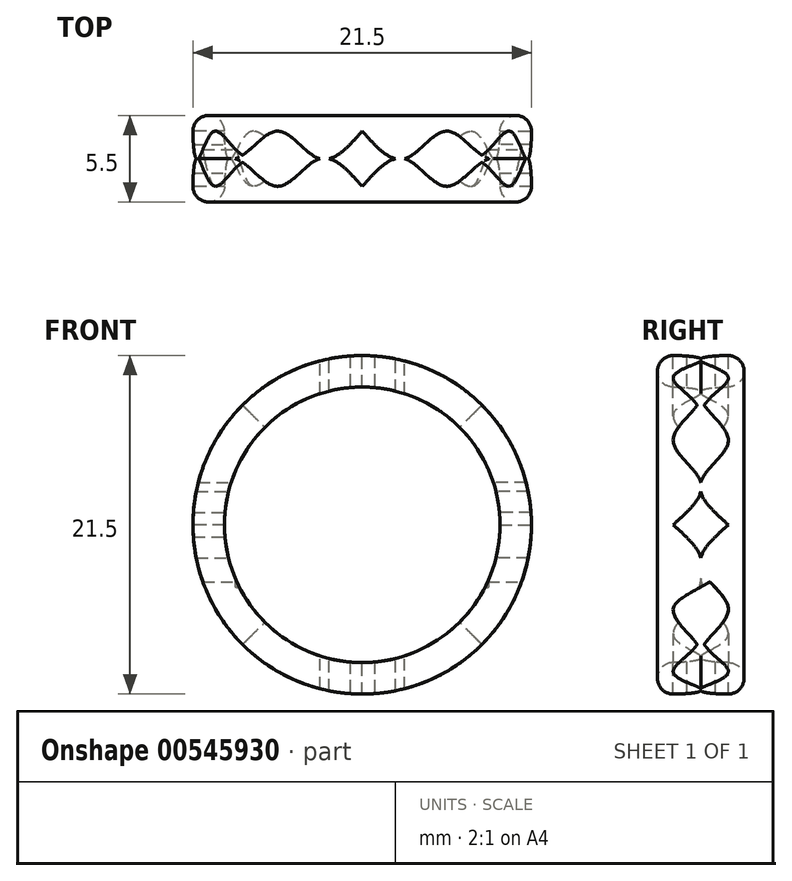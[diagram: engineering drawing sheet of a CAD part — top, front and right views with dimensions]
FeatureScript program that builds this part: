
annotation { "Feature Type Name" : "Feature", "Feature Type Description" : "" }
export const myFeature = defineFeature(function(context is Context, id is Id, definition is map)
    precondition{}
    {
        {
            var Q0;
            Q0=qCreatedBy(makeId("Front.planeOp"),FACE);
            var sketch = newSketch(context, id + "F0", { "sketchPlane" : qUnion([Q0])});
            skCircle(sketch, "E0", {"center": v(0, 0) * mm, "radius": 8.75 * mm});
            skCircle(sketch, "E1", {"center": v(0, 0) * mm, "radius": 10.75 * mm});
            skSolve(sketch);
        }
        {
            var Q0;
            Q0=makeQuery(id+"F0.imprint","IMPRINT",FACE,{"disambiguationData":[TD([[makeQuery(id+"F0.imprint","IMPRINT",EDGE,{"derivedFrom":sQuery(id+"F0.wireOp",EDGE,"E0")}),-1.0]])]});
            extrude(context, id + "F1", {"entities" : qUnion([Q0]), "depth" : 3.75 * mm, "offsetDistance" : 25 * mm, "hasSecondDirection" : true, "secondDirectionOppositeDirection" : true, "secondDirectionDepth" : 3.75 * mm});
        }
        {
            var Q0;
            Q0=makeQuery(id+"F1.opExtrude","CAP_EDGE",EDGE,{"disambiguationData":[OSD([sQuery(id+"F0.wireOp",EDGE,"E1")])],"isStart":false});
            var Q1;
            Q1=makeQuery(id+"F1.opExtrude","CAP_EDGE",EDGE,{"disambiguationData":[OSD([sQuery(id+"F0.wireOp",EDGE,"E1")])],"isStart":true});
            fillet(context, id + "F2", {"entities" : qUnion([Q0, Q1]), "radius" : 2 * mm, "tangentPropagation" : true, "allowEdgeOverflow" : false});
        }
        {
            var Q0;
            Q0=makeQuery(id+"F2.opFillet","BLEND_EDGE",EDGE,{"blendedFrom":[makeQuery(id+"F1.opExtrude","CAP_EDGE",EDGE,{"disambiguationData":[OSD([sQuery(id+"F0.wireOp",EDGE,"E1")])],"isStart":false}),makeQuery(id+"F1.opExtrude","SWEPT_FACE",FACE,{"disambiguationData":[OSD([sQuery(id+"F0.wireOp",EDGE,"E0")])]})],"blendedInto":[makeQuery(id+"F1.opExtrude","SWEPT_FACE",FACE,{"disambiguationData":[OSD([sQuery(id+"F0.wireOp",EDGE,"E0")])]})]});
            var Q1;
            Q1=makeQuery(id+"F2.opFillet","BLEND_EDGE",EDGE,{"blendedFrom":[makeQuery(id+"F1.opExtrude","CAP_EDGE",EDGE,{"disambiguationData":[OSD([sQuery(id+"F0.wireOp",EDGE,"E1")])],"isStart":true}),makeQuery(id+"F1.opExtrude","SWEPT_FACE",FACE,{"disambiguationData":[OSD([sQuery(id+"F0.wireOp",EDGE,"E0")])]})],"blendedInto":[makeQuery(id+"F1.opExtrude","SWEPT_FACE",FACE,{"disambiguationData":[OSD([sQuery(id+"F0.wireOp",EDGE,"E0")])]})]});
            fillet(context, id + "F3", {"entities" : qUnion([Q0, Q1]), "radius" : 1 * mm, "tangentPropagation" : true, "allowEdgeOverflow" : false});
        }
        {
            var Q0;
            Q0=qCreatedBy(makeId("Right.planeOp"),FACE);
            var sketch = newSketch(context, id + "F4", { "sketchPlane" : qUnion([Q0])});
            skLineSegment(sketch, "E2.bottom", {"start": v(1.75, -10.75) * mm, "end": v(-1.75, -10.75) * mm});
            skLineSegment(sketch, "E2.top", {"start": v(1.75, 10.75) * mm, "end": v(-1.75, 10.75) * mm});
            skLineSegment(sketch, "E2.left", {"start": v(1.75, -10.75) * mm, "end": v(1.75, 10.75) * mm});
            skLineSegment(sketch, "E2.right", {"start": v(-1.75, -10.75) * mm, "end": v(-1.75, 10.75) * mm});
            skPoint(sketch, "E2.middle", {"position": v(0, 0) * mm});
            skPoint(sketch, "E3", {"position": v(1.75, 5.38) * mm});
            skPoint(sketch, "E4", {"position": v(1.75, 2.69) * mm});
            skPoint(sketch, "E5", {"position": v(1.75, 8.06) * mm});
            skPoint(sketch, "E6.MirrorP", {"position": v(-1.75, 2.69) * mm});
            skPoint(sketch, "E7.MirrorP", {"position": v(-1.75, 5.38) * mm});
            skPoint(sketch, "E8.MirrorP", {"position": v(-1.75, 8.06) * mm});
            skPoint(sketch, "E9.MirrorP", {"position": v(-1.75, -2.69) * mm});
            skPoint(sketch, "E10.MirrorP", {"position": v(-1.75, -5.38) * mm});
            skPoint(sketch, "E11.MirrorP", {"position": v(-1.75, -8.06) * mm});
            skPoint(sketch, "E12.MirrorP", {"position": v(1.75, -8.06) * mm});
            skPoint(sketch, "E13.MirrorP", {"position": v(1.75, -5.38) * mm});
            skPoint(sketch, "E14.MirrorP", {"position": v(1.75, -2.69) * mm});
            skPoint(sketch, "E15", {"position": v(0, 8.06) * mm});
            skPoint(sketch, "E16", {"position": v(0, 5.38) * mm});
            skPoint(sketch, "E17", {"position": v(0, 2.69) * mm});
            skFitSpline(sketch, "E18", {"points": [v(0, 10.75) * mm, v(-1.75, 8.06) * mm, v(1.75, 5.38) * mm, v(-1.75, 2.69) * mm, v(0, 0) * mm], "startDerivative": vector(-14.8, -12.07) * mm, "endDerivative": vector(14.8, -12.08) * mm});
            skFitSpline(sketch, "E19.MirrorCS", {"points": [v(0, 10.75) * mm, v(1.75, 8.06) * mm, v(-1.75, 5.38) * mm, v(1.75, 2.69) * mm, v(0, 0) * mm], "startDerivative": vector(14.8, -12.07) * mm, "endDerivative": vector(-14.8, -12.08) * mm});
            skFitSpline(sketch, "E20.MirrorCS", {"points": [v(0, -10.75) * mm, v(-1.75, -8.06) * mm, v(1.75, -5.38) * mm, v(-1.75, -2.69) * mm, v(0, 0) * mm], "startDerivative": vector(-14.8, 12.07) * mm, "endDerivative": vector(14.8, 12.08) * mm});
            skFitSpline(sketch, "E21.MirrorCS", {"points": [v(0, -10.75) * mm, v(1.75, -8.06) * mm, v(-1.75, -5.38) * mm, v(1.75, -2.69) * mm, v(0, 0) * mm], "startDerivative": vector(14.8, 12.07) * mm, "endDerivative": vector(-14.8, 12.08) * mm});
            skFitSpline(sketch, "E22", {"points": [v(1.75, 10.75) * mm, v(0, 8.06) * mm, v(1.75, 5.38) * mm, v(0, 2.69) * mm, v(1.75, 0) * mm], "startDerivative": vector(-12, -10.75) * mm, "endDerivative": vector(12, -10.75) * mm});
            skFitSpline(sketch, "E23", {"points": [v(-1.75, 10.75) * mm, v(0, 8.06) * mm, v(-1.75, 5.38) * mm, v(0, 2.69) * mm, v(-1.75, 0) * mm], "startDerivative": vector(12, -10.75) * mm, "endDerivative": vector(-12, -10.75) * mm});
            skFitSpline(sketch, "E24.MirrorCS", {"points": [v(-1.75, -10.75) * mm, v(0, -8.06) * mm, v(-1.75, -5.38) * mm, v(0, -2.69) * mm, v(-1.75, 0) * mm], "startDerivative": vector(12, 10.75) * mm, "endDerivative": vector(-12, 10.75) * mm});
            skFitSpline(sketch, "E25.MirrorCS", {"points": [v(1.75, -10.75) * mm, v(0, -8.06) * mm, v(1.75, -5.38) * mm, v(0, -2.69) * mm, v(1.75, 0) * mm], "startDerivative": vector(-12, 10.75) * mm, "endDerivative": vector(12, 10.75) * mm});
            skSolve(sketch);
        }
        {
            var Q0;
            Q0=qCreatedBy(makeId("Top.planeOp"),FACE);
            cPlane(context, id + "F5", {"entities" : qUnion([Q0]), "cplaneType" : CPlaneType.OFFSET, "offset" : (21.5 / 2) * mm, "width" : 150 * mm, "height" : 150 * mm});
        }
        {
            var Q0;
            Q0=qCreatedBy(id+"F5.planeOp",FACE);
            var sketch = newSketch(context, id + "F6", { "sketchPlane" : qUnion([Q0])});
            skPoint(sketch, "E26", {"position": v(0, 0) * mm});
            skPoint(sketch, "E27", {"position": v(-10.75, 0) * mm});
            skPoint(sketch, "E28", {"position": v(0, -1.75) * mm});
            skPoint(sketch, "E29", {"position": v(-10.75, -1.75) * mm});
            skPoint(sketch, "E30", {"position": v(-10.75, 1.75) * mm});
            skPoint(sketch, "E31", {"position": v(0, 1.75) * mm});
            skPoint(sketch, "E32", {"position": v(-5.38, 1.75) * mm});
            skPoint(sketch, "E33", {"position": v(-8.06, 1.75) * mm});
            skPoint(sketch, "E34", {"position": v(-8.06, -1.75) * mm});
            skPoint(sketch, "E35", {"position": v(-5.38, -1.75) * mm});
            skPoint(sketch, "E36", {"position": v(-2.69, 1.75) * mm});
            skPoint(sketch, "E37", {"position": v(-2.69, -1.75) * mm});
            skPoint(sketch, "E38.MirrorP", {"position": v(10.75, -1.75) * mm});
            skPoint(sketch, "E39.MirrorP", {"position": v(10.75, 1.75) * mm});
            skPoint(sketch, "E40.MirrorP", {"position": v(10.75, 0) * mm});
            skPoint(sketch, "E41.MirrorP", {"position": v(8.06, -1.75) * mm});
            skPoint(sketch, "E42.MirrorP", {"position": v(8.06, 1.75) * mm});
            skPoint(sketch, "E43.MirrorP", {"position": v(5.38, 1.75) * mm});
            skPoint(sketch, "E44.MirrorP", {"position": v(2.69, 1.75) * mm});
            skPoint(sketch, "E45.MirrorP", {"position": v(2.69, -1.75) * mm});
            skPoint(sketch, "E46.MirrorP", {"position": v(5.38, -1.75) * mm});
            skPoint(sketch, "E47", {"position": v(-8.06, 0) * mm});
            skPoint(sketch, "E48", {"position": v(-5.38, 0) * mm});
            skPoint(sketch, "E49", {"position": v(-2.69, 0) * mm});
            skPoint(sketch, "E50.MirrorP", {"position": v(2.69, 0) * mm});
            skPoint(sketch, "E51.MirrorP", {"position": v(5.38, 0) * mm});
            skPoint(sketch, "E52.MirrorP", {"position": v(8.06, 0) * mm});
            skFitSpline(sketch, "E53", {"points": [v(0, 0) * mm, v(-2.69, -1.75) * mm, v(-5.38, 1.75) * mm, v(-8.06, -1.75) * mm, v(-10.75, 1.75) * mm], "startDerivative": vector(-12.6, -15.44) * mm, "endDerivative": vector(-10.32, 23.06) * mm});
            skFitSpline(sketch, "E54", {"points": [v(-10.75, -1.75) * mm, v(-8.06, 1.75) * mm, v(-5.38, -1.75) * mm, v(-2.69, 1.75) * mm, v(0, 0) * mm], "startDerivative": vector(13.87, 22.06) * mm, "endDerivative": vector(12.03, -14.48) * mm});
            skFitSpline(sketch, "E55", {"points": [v(0, 1.75) * mm, v(-2.69, 0) * mm, v(-5.38, 1.75) * mm, v(-8.06, 0) * mm, v(-10.75, 1.75) * mm], "startDerivative": vector(-10.75, -12) * mm, "endDerivative": vector(-10.75, 12) * mm});
            skFitSpline(sketch, "E56", {"points": [v(-10.75, -1.75) * mm, v(-8.06, 0) * mm, v(-5.38, -1.75) * mm, v(-2.69, 0) * mm, v(0, -1.75) * mm], "startDerivative": vector(10.75, 12) * mm, "endDerivative": vector(10.75, -12) * mm});
            skFitSpline(sketch, "E57.MirrorCS", {"points": [v(10.75, -1.75) * mm, v(8.06, 1.75) * mm, v(5.38, -1.75) * mm, v(2.69, 1.75) * mm, v(0, 0) * mm], "startDerivative": vector(-13.87, 22.06) * mm, "endDerivative": vector(-12.03, -14.48) * mm});
            skFitSpline(sketch, "E58.MirrorCS", {"points": [v(0, 0) * mm, v(2.69, -1.75) * mm, v(5.38, 1.75) * mm, v(8.06, -1.75) * mm, v(10.75, 1.75) * mm], "startDerivative": vector(12.6, -15.44) * mm, "endDerivative": vector(10.32, 23.06) * mm});
            skFitSpline(sketch, "E59.MirrorCS", {"points": [v(0, 1.75) * mm, v(2.69, 0) * mm, v(5.38, 1.75) * mm, v(8.06, 0) * mm, v(10.75, 1.75) * mm], "startDerivative": vector(10.75, -12) * mm, "endDerivative": vector(10.75, 12) * mm});
            skFitSpline(sketch, "E60.MirrorCS", {"points": [v(10.75, -1.75) * mm, v(8.06, 0) * mm, v(5.38, -1.75) * mm, v(2.69, 0) * mm, v(0, -1.75) * mm], "startDerivative": vector(-10.75, 12) * mm, "endDerivative": vector(-10.75, -12) * mm});
            skPoint(sketch, "E61", {"position": v(-4.48, -0.95) * mm});
            skPoint(sketch, "E62", {"position": v(-6.28, -0.95) * mm});
            skPoint(sketch, "E63.MirrorP", {"position": v(-6.28, 0.95) * mm});
            skPoint(sketch, "E64.MirrorP", {"position": v(-4.48, 0.95) * mm});
            skPoint(sketch, "E65.MirrorP", {"position": v(4.48, -0.95) * mm});
            skPoint(sketch, "E66.MirrorP", {"position": v(6.28, -0.95) * mm});
            skPoint(sketch, "E67.MirrorP", {"position": v(4.48, 0.95) * mm});
            skPoint(sketch, "E68.MirrorP", {"position": v(6.28, 0.95) * mm});
            skPoint(sketch, "E69", {"position": v(-5.38, -0.95) * mm});
            skLineSegment(sketch, "E70.left", {"start": v(10.75, -0.25) * mm, "end": v(10.75, 0.25) * mm});
            skLineSegment(sketch, "E70.right", {"start": v(-10.75, -0.25) * mm, "end": v(-10.75, 0.25) * mm});
            skSolve(sketch);
        }
        {
            var Q0;
            {var subQ3=sQuery(id+"F6.wireOp",EDGE,"E55");var subQ5=sQuery(id+"F6.wireOp",EDGE,"E59.MirrorCS");var subQ6=makeQuery(id+"F6.imprint","INTERSECT",VERTEX,{"derivedFrom":[subQ3,subQ5]});Q0=makeQuery(id+"F6.imprint","IMPRINT",FACE,{"disambiguationData":[TD([[makeQuery(id+"F6.imprint","IMPRINT",EDGE,{"disambiguationData":[TD([[subQ6,-1.0]])],"derivedFrom":subQ3}),1.0]])]});}
            var Q1;
            {var subQ1=sQuery(id+"F6.wireOp",EDGE,"E57.MirrorCS");var subQ3=sQuery(id+"F6.wireOp",EDGE,"E59.MirrorCS");var subQ4=makeQuery(id+"F6.imprint","INTERSECT",VERTEX,{"disambiguationData":[OD(3.0)],"derivedFrom":[subQ1,subQ3]});Q1=makeQuery(id+"F6.imprint","IMPRINT",FACE,{"disambiguationData":[TD([[makeQuery(id+"F6.imprint","IMPRINT",EDGE,{"disambiguationData":[TD([[subQ4,-1.0]])],"derivedFrom":subQ3}),-1.0]])]});}
            var Q2;
            {var subQ3=sQuery(id+"F6.wireOp",EDGE,"E56");var subQ5=sQuery(id+"F6.wireOp",EDGE,"E60.MirrorCS");var subQ6=makeQuery(id+"F6.imprint","INTERSECT",VERTEX,{"derivedFrom":[subQ3,subQ5]});Q2=makeQuery(id+"F6.imprint","IMPRINT",FACE,{"disambiguationData":[TD([[makeQuery(id+"F6.imprint","IMPRINT",EDGE,{"disambiguationData":[TD([[subQ6,1.0]])],"derivedFrom":subQ3}),1.0]])]});}
            var Q3;
            {var subQ0=sQuery(id+"F6.wireOp",EDGE,"E54");var subQ5=sQuery(id+"F6.wireOp",EDGE,"E55");var subQ7=makeQuery(id+"F6.imprint","INTERSECT",VERTEX,{"disambiguationData":[OD(3.0)],"derivedFrom":[subQ0,subQ5]});Q3=makeQuery(id+"F6.imprint","IMPRINT",FACE,{"disambiguationData":[TD([[makeQuery(id+"F6.imprint","IMPRINT",EDGE,{"disambiguationData":[TD([[subQ7,-1.0]])],"derivedFrom":subQ5}),1.0]])]});}
            var Q4;
            {var subQ0=sQuery(id+"F6.wireOp",EDGE,"E56");var subQ1=sQuery(id+"F6.wireOp",EDGE,"E53");var subQ2=makeQuery(id+"F6.imprint","INTERSECT",VERTEX,{"disambiguationData":[OD(1.0)],"derivedFrom":[subQ1,subQ0]});Q4=makeQuery(id+"F6.imprint","IMPRINT",FACE,{"disambiguationData":[TD([[makeQuery(id+"F6.imprint","IMPRINT",EDGE,{"disambiguationData":[TD([[subQ2,-1.0]])],"derivedFrom":subQ1}),-1.0]])]});}
            var Q5;
            {var subQ0=sQuery(id+"F6.wireOp",EDGE,"E55");var subQ1=sQuery(id+"F6.wireOp",EDGE,"E53");var subQ2=makeQuery(id+"F6.imprint","INTERSECT",VERTEX,{"disambiguationData":[OD(1.0)],"derivedFrom":[subQ1,subQ0]});Q5=makeQuery(id+"F6.imprint","IMPRINT",FACE,{"disambiguationData":[TD([[makeQuery(id+"F6.imprint","IMPRINT",EDGE,{"disambiguationData":[TD([[subQ2,1.0]])],"derivedFrom":subQ1}),-1.0]])]});}
            var Q6;
            {var subQ0=sQuery(id+"F6.wireOp",EDGE,"E56");var subQ1=sQuery(id+"F6.wireOp",EDGE,"E53");var subQ2=makeQuery(id+"F6.imprint","INTERSECT",VERTEX,{"disambiguationData":[OD(1.0)],"derivedFrom":[subQ1,subQ0]});Q6=makeQuery(id+"F6.imprint","IMPRINT",FACE,{"disambiguationData":[TD([[makeQuery(id+"F6.imprint","IMPRINT",EDGE,{"disambiguationData":[TD([[subQ2,-1.0]])],"derivedFrom":subQ1}),1.0]])]});}
            var Q7;
            {var subQ0=sQuery(id+"F6.wireOp",EDGE,"E59.MirrorCS");var subQ1=sQuery(id+"F6.wireOp",EDGE,"E57.MirrorCS");var subQ2=makeQuery(id+"F6.imprint","INTERSECT",VERTEX,{"disambiguationData":[OD(2.0)],"derivedFrom":[subQ1,subQ0]});Q7=makeQuery(id+"F6.imprint","IMPRINT",FACE,{"disambiguationData":[TD([[makeQuery(id+"F6.imprint","IMPRINT",EDGE,{"disambiguationData":[TD([[subQ2,1.0]])],"derivedFrom":subQ1}),1.0]])]});}
            var Q8;
            {var subQ0=sQuery(id+"F6.wireOp",EDGE,"E59.MirrorCS");var subQ1=sQuery(id+"F6.wireOp",EDGE,"E57.MirrorCS");var subQ2=makeQuery(id+"F6.imprint","INTERSECT",VERTEX,{"disambiguationData":[OD(2.0)],"derivedFrom":[subQ1,subQ0]});Q8=makeQuery(id+"F6.imprint","IMPRINT",FACE,{"disambiguationData":[TD([[makeQuery(id+"F6.imprint","IMPRINT",EDGE,{"disambiguationData":[TD([[subQ2,1.0]])],"derivedFrom":subQ1}),-1.0]])]});}
            var Q9;
            {var subQ0=sQuery(id+"F6.wireOp",EDGE,"E60.MirrorCS");var subQ1=sQuery(id+"F6.wireOp",EDGE,"E57.MirrorCS");var subQ2=makeQuery(id+"F6.imprint","INTERSECT",VERTEX,{"disambiguationData":[OD(2.0)],"derivedFrom":[subQ1,subQ0]});Q9=makeQuery(id+"F6.imprint","IMPRINT",FACE,{"disambiguationData":[TD([[makeQuery(id+"F6.imprint","IMPRINT",EDGE,{"disambiguationData":[TD([[subQ2,-1.0]])],"derivedFrom":subQ1}),1.0]])]});}
            var Q10;
            {var subQ0=sQuery(id+"F6.wireOp",EDGE,"E55");var subQ1=sQuery(id+"F6.wireOp",EDGE,"E53");var subQ2=makeQuery(id+"F6.imprint","INTERSECT",VERTEX,{"disambiguationData":[OD(2.0)],"derivedFrom":[subQ1,subQ0]});Q10=makeQuery(id+"F6.imprint","IMPRINT",FACE,{"disambiguationData":[TD([[makeQuery(id+"F6.imprint","IMPRINT",EDGE,{"disambiguationData":[TD([[subQ2,-1.0]])],"derivedFrom":subQ1}),-1.0]])]});}
            var Q11;
            {var subQ0=sQuery(id+"F6.wireOp",EDGE,"E56");var subQ1=sQuery(id+"F6.wireOp",EDGE,"E53");var subQ2=makeQuery(id+"F6.imprint","INTERSECT",VERTEX,{"disambiguationData":[OD(2.0)],"derivedFrom":[subQ1,subQ0]});Q11=makeQuery(id+"F6.imprint","IMPRINT",FACE,{"disambiguationData":[TD([[makeQuery(id+"F6.imprint","IMPRINT",EDGE,{"disambiguationData":[TD([[subQ2,1.0]])],"derivedFrom":subQ1}),-1.0]])]});}
            var Q12;
            {var subQ0=sQuery(id+"F6.wireOp",EDGE,"E56");var subQ1=sQuery(id+"F6.wireOp",EDGE,"E53");var subQ2=makeQuery(id+"F6.imprint","INTERSECT",VERTEX,{"disambiguationData":[OD(2.0)],"derivedFrom":[subQ1,subQ0]});Q12=makeQuery(id+"F6.imprint","IMPRINT",FACE,{"disambiguationData":[TD([[makeQuery(id+"F6.imprint","IMPRINT",EDGE,{"disambiguationData":[TD([[subQ2,1.0]])],"derivedFrom":subQ1}),1.0]])]});}
            var Q13;
            {var subQ0=sQuery(id+"F6.wireOp",EDGE,"E60.MirrorCS");var subQ1=sQuery(id+"F6.wireOp",EDGE,"E57.MirrorCS");var subQ2=makeQuery(id+"F6.imprint","INTERSECT",VERTEX,{"disambiguationData":[OD(1.0)],"derivedFrom":[subQ1,subQ0]});Q13=makeQuery(id+"F6.imprint","IMPRINT",FACE,{"disambiguationData":[TD([[makeQuery(id+"F6.imprint","IMPRINT",EDGE,{"disambiguationData":[TD([[subQ2,1.0]])],"derivedFrom":subQ1}),1.0]])]});}
            var Q14;
            {var subQ0=sQuery(id+"F6.wireOp",EDGE,"E59.MirrorCS");var subQ1=sQuery(id+"F6.wireOp",EDGE,"E57.MirrorCS");var subQ2=makeQuery(id+"F6.imprint","INTERSECT",VERTEX,{"disambiguationData":[OD(1.0)],"derivedFrom":[subQ1,subQ0]});Q14=makeQuery(id+"F6.imprint","IMPRINT",FACE,{"disambiguationData":[TD([[makeQuery(id+"F6.imprint","IMPRINT",EDGE,{"disambiguationData":[TD([[subQ2,-1.0]])],"derivedFrom":subQ1}),1.0]])]});}
            var Q15;
            {var subQ0=sQuery(id+"F6.wireOp",EDGE,"E59.MirrorCS");var subQ1=sQuery(id+"F6.wireOp",EDGE,"E57.MirrorCS");var subQ2=makeQuery(id+"F6.imprint","INTERSECT",VERTEX,{"disambiguationData":[OD(1.0)],"derivedFrom":[subQ1,subQ0]});Q15=makeQuery(id+"F6.imprint","IMPRINT",FACE,{"disambiguationData":[TD([[makeQuery(id+"F6.imprint","IMPRINT",EDGE,{"disambiguationData":[TD([[subQ2,-1.0]])],"derivedFrom":subQ1}),-1.0]])]});}
            var Q16;
            {var subQ3=sQuery(id+"F6.wireOp",EDGE,"E53");var subQ5=sQuery(id+"F6.wireOp",EDGE,"E55");var subQ9=makeQuery(id+"F6.imprint","INTERSECT",VERTEX,{"disambiguationData":[OD(1.0)],"derivedFrom":[subQ3,subQ5]});Q16=makeQuery(id+"F6.imprint","IMPRINT",FACE,{"disambiguationData":[TD([[makeQuery(id+"F6.imprint","IMPRINT",EDGE,{"disambiguationData":[TD([[subQ9,1.0]])],"derivedFrom":subQ3}),1.0]])]});}
            var Q17;
            {var subQ3=sQuery(id+"F6.wireOp",EDGE,"E57.MirrorCS");var subQ5=sQuery(id+"F6.wireOp",EDGE,"E60.MirrorCS");var subQ6=makeQuery(id+"F6.imprint","INTERSECT",VERTEX,{"disambiguationData":[OD(1.0)],"derivedFrom":[subQ3,subQ5]});Q17=makeQuery(id+"F6.imprint","IMPRINT",FACE,{"disambiguationData":[TD([[makeQuery(id+"F6.imprint","IMPRINT",EDGE,{"disambiguationData":[TD([[subQ6,1.0]])],"derivedFrom":subQ3}),-1.0]])]});}
            var Q18;
            {var subQ0=sQuery(id+"F6.wireOp",EDGE,"E56");var subQ1=sQuery(id+"F6.wireOp",EDGE,"E53");var subQ2=makeQuery(id+"F6.imprint","INTERSECT",VERTEX,{"disambiguationData":[OD(0.0)],"derivedFrom":[subQ1,subQ0]});Q18=makeQuery(id+"F6.imprint","IMPRINT",FACE,{"disambiguationData":[TD([[makeQuery(id+"F6.imprint","IMPRINT",EDGE,{"disambiguationData":[TD([[subQ2,1.0]])],"derivedFrom":subQ1}),-1.0]])]});}
            var Q19;
            Q19=makeQuery(id+"FG5QF2xXgg8FTiy_1.imprint","IMPRINT",FACE,{"disambiguationData":[TD([[makeQuery(id+"FG5QF2xXgg8FTiy_1.imprint","IMPRINT",EDGE,{"derivedFrom":sQuery(id+"FG5QF2xXgg8FTiy_1.wireOp",EDGE,"0z52b0YR-wwrJ-KUp3-x6KW-sjqR8KIbK8CL.bottom")}),-1.0]])]});
            var Q20;
            {var subQ0=sQuery(id+"F6.wireOp",EDGE,"E60.MirrorCS");var subQ1=sQuery(id+"F6.wireOp",EDGE,"E58.MirrorCS");var subQ2=makeQuery(id+"F6.imprint","INTERSECT",VERTEX,{"disambiguationData":[OD(0.0)],"derivedFrom":[subQ1,subQ0]});Q20=makeQuery(id+"F6.imprint","IMPRINT",FACE,{"disambiguationData":[TD([[makeQuery(id+"F6.imprint","IMPRINT",EDGE,{"disambiguationData":[TD([[subQ2,1.0]])],"derivedFrom":subQ1}),1.0]])]});}
            var Q21;
            {var subQ0=sQuery(id+"F6.wireOp",EDGE,"E56");var subQ1=sQuery(id+"F6.wireOp",EDGE,"E54");var subQ2=makeQuery(id+"F6.imprint","INTERSECT",VERTEX,{"disambiguationData":[OD(1.0)],"derivedFrom":[subQ1,subQ0]});Q21=makeQuery(id+"F6.imprint","IMPRINT",FACE,{"disambiguationData":[TD([[makeQuery(id+"F6.imprint","IMPRINT",EDGE,{"disambiguationData":[TD([[subQ2,1.0]])],"derivedFrom":subQ1}),1.0]])]});}
            var Q22;
            {var subQ0=sQuery(id+"F6.wireOp",EDGE,"E59.MirrorCS");var subQ1=sQuery(id+"F6.wireOp",EDGE,"E58.MirrorCS");var subQ2=makeQuery(id+"F6.imprint","INTERSECT",VERTEX,{"disambiguationData":[OD(1.0)],"derivedFrom":[subQ1,subQ0]});Q22=makeQuery(id+"F6.imprint","IMPRINT",FACE,{"disambiguationData":[TD([[makeQuery(id+"F6.imprint","IMPRINT",EDGE,{"disambiguationData":[TD([[subQ2,1.0]])],"derivedFrom":subQ1}),-1.0]])]});}
            var Q23;
            {var subQ0=sQuery(id+"F6.wireOp",EDGE,"E60.MirrorCS");var subQ1=sQuery(id+"F6.wireOp",EDGE,"E58.MirrorCS");var subQ2=makeQuery(id+"F6.imprint","INTERSECT",VERTEX,{"disambiguationData":[OD(1.0)],"derivedFrom":[subQ1,subQ0]});Q23=makeQuery(id+"F6.imprint","IMPRINT",FACE,{"disambiguationData":[TD([[makeQuery(id+"F6.imprint","IMPRINT",EDGE,{"disambiguationData":[TD([[subQ2,-1.0]])],"derivedFrom":subQ1}),1.0]])]});}
            var Q24;
            {var subQ0=sQuery(id+"F6.wireOp",EDGE,"E60.MirrorCS");var subQ1=sQuery(id+"F6.wireOp",EDGE,"E58.MirrorCS");var subQ2=makeQuery(id+"F6.imprint","INTERSECT",VERTEX,{"disambiguationData":[OD(2.0)],"derivedFrom":[subQ1,subQ0]});Q24=makeQuery(id+"F6.imprint","IMPRINT",FACE,{"disambiguationData":[TD([[makeQuery(id+"F6.imprint","IMPRINT",EDGE,{"disambiguationData":[TD([[subQ2,1.0]])],"derivedFrom":subQ1}),1.0]])]});}
            var Q25;
            {var subQ0=sQuery(id+"F6.wireOp",EDGE,"E55");var subQ1=sQuery(id+"F6.wireOp",EDGE,"E54");var subQ2=makeQuery(id+"F6.imprint","INTERSECT",VERTEX,{"disambiguationData":[OD(2.0)],"derivedFrom":[subQ1,subQ0]});Q25=makeQuery(id+"F6.imprint","IMPRINT",FACE,{"disambiguationData":[TD([[makeQuery(id+"F6.imprint","IMPRINT",EDGE,{"disambiguationData":[TD([[subQ2,1.0]])],"derivedFrom":subQ1}),-1.0]])]});}
            var Q26;
            {var subQ0=sQuery(id+"F6.wireOp",EDGE,"E55");var subQ1=sQuery(id+"F6.wireOp",EDGE,"E54");var subQ2=makeQuery(id+"F6.imprint","INTERSECT",VERTEX,{"disambiguationData":[OD(1.0)],"derivedFrom":[subQ1,subQ0]});Q26=makeQuery(id+"F6.imprint","IMPRINT",FACE,{"disambiguationData":[TD([[makeQuery(id+"F6.imprint","IMPRINT",EDGE,{"disambiguationData":[TD([[subQ2,-1.0]])],"derivedFrom":subQ1}),-1.0]])]});}
            extrude(context, id + "F7", {"entities" : qUnion([Q0, Q1, Q2, Q3, Q4, Q5, Q6, Q7, Q8, Q9, Q10, Q11, Q12, Q13, Q14, Q15, Q16, Q17, Q18, Q19, Q20, Q21, Q22, Q23, Q24, Q25, Q26]), "operationType" : NewBodyOperationType.REMOVE, "oppositeDirection" : true, "depth" : 25 * mm, "offsetDistance" : 25 * mm});
        }
        {
            var Q0;
            {var subQ0=sQuery(id+"F4.wireOp",EDGE,"E19.MirrorCS");var subQ5=sQuery(id+"F4.wireOp",EDGE,"E22");var subQ6=makeQuery(id+"F4.imprint","INTERSECT",VERTEX,{"disambiguationData":[OD(3.0)],"derivedFrom":[subQ0,subQ5]});Q0=makeQuery(id+"F4.imprint","IMPRINT",FACE,{"disambiguationData":[TD([[makeQuery(id+"F4.imprint","IMPRINT",EDGE,{"disambiguationData":[TD([[subQ6,1.0]])],"derivedFrom":subQ5}),-1.0]])]});}
            var Q1;
            {var subQ1=sQuery(id+"F4.wireOp",EDGE,"E18");var subQ3=sQuery(id+"F4.wireOp",EDGE,"E23");var subQ4=makeQuery(id+"F4.imprint","INTERSECT",VERTEX,{"disambiguationData":[OD(3.0)],"derivedFrom":[subQ1,subQ3]});Q1=makeQuery(id+"F4.imprint","IMPRINT",FACE,{"disambiguationData":[TD([[makeQuery(id+"F4.imprint","IMPRINT",EDGE,{"disambiguationData":[TD([[subQ4,-1.0]])],"derivedFrom":subQ3}),1.0]])]});}
            var Q2;
            {var subQ1=sQuery(id+"F4.wireOp",EDGE,"E20.MirrorCS");var subQ3=sQuery(id+"F4.wireOp",EDGE,"E24.MirrorCS");var subQ4=makeQuery(id+"F4.imprint","INTERSECT",VERTEX,{"disambiguationData":[OD(3.0)],"derivedFrom":[subQ1,subQ3]});Q2=makeQuery(id+"F4.imprint","IMPRINT",FACE,{"disambiguationData":[TD([[makeQuery(id+"F4.imprint","IMPRINT",EDGE,{"disambiguationData":[TD([[subQ4,1.0]])],"derivedFrom":subQ3}),-1.0]])]});}
            var Q3;
            {var subQ1=sQuery(id+"F4.wireOp",EDGE,"E19.MirrorCS");var subQ3=sQuery(id+"F4.wireOp",EDGE,"E22");var subQ4=makeQuery(id+"F4.imprint","INTERSECT",VERTEX,{"disambiguationData":[OD(3.0)],"derivedFrom":[subQ1,subQ3]});Q3=makeQuery(id+"F4.imprint","IMPRINT",FACE,{"disambiguationData":[TD([[makeQuery(id+"F4.imprint","IMPRINT",EDGE,{"disambiguationData":[TD([[subQ4,-1.0]])],"derivedFrom":subQ3}),-1.0]])]});}
            var Q4;
            {var subQ0=sQuery(id+"F4.wireOp",EDGE,"E19.MirrorCS");var subQ1=sQuery(id+"F4.wireOp",EDGE,"E18");var subQ2=makeQuery(id+"F4.imprint","INTERSECT",VERTEX,{"disambiguationData":[OD(1.0)],"derivedFrom":[subQ1,subQ0]});Q4=makeQuery(id+"F4.imprint","IMPRINT",FACE,{"disambiguationData":[TD([[makeQuery(id+"F4.imprint","IMPRINT",EDGE,{"disambiguationData":[TD([[subQ2,-1.0]])],"derivedFrom":subQ1}),1.0]])]});}
            var Q5;
            {var subQ0=sQuery(id+"F4.wireOp",EDGE,"E19.MirrorCS");var subQ1=sQuery(id+"F4.wireOp",EDGE,"E18");var subQ2=makeQuery(id+"F4.imprint","INTERSECT",VERTEX,{"disambiguationData":[OD(1.0)],"derivedFrom":[subQ1,subQ0]});Q5=makeQuery(id+"F4.imprint","IMPRINT",FACE,{"disambiguationData":[TD([[makeQuery(id+"F4.imprint","IMPRINT",EDGE,{"disambiguationData":[TD([[subQ2,-1.0]])],"derivedFrom":subQ1}),-1.0]])]});}
            var Q6;
            {var subQ0=sQuery(id+"F4.wireOp",EDGE,"E22");var subQ1=sQuery(id+"F4.wireOp",EDGE,"E18");var subQ2=makeQuery(id+"F4.imprint","INTERSECT",VERTEX,{"derivedFrom":[subQ1,subQ0]});Q6=makeQuery(id+"F4.imprint","IMPRINT",FACE,{"disambiguationData":[TD([[makeQuery(id+"F4.imprint","IMPRINT",EDGE,{"disambiguationData":[TD([[subQ2,-1.0]])],"derivedFrom":subQ1}),1.0]])]});}
            var Q7;
            {var subQ0=sQuery(id+"F4.wireOp",EDGE,"E21.MirrorCS");var subQ1=sQuery(id+"F4.wireOp",EDGE,"E20.MirrorCS");var subQ2=makeQuery(id+"F4.imprint","INTERSECT",VERTEX,{"disambiguationData":[OD(1.0)],"derivedFrom":[subQ1,subQ0]});Q7=makeQuery(id+"F4.imprint","IMPRINT",FACE,{"disambiguationData":[TD([[makeQuery(id+"F4.imprint","IMPRINT",EDGE,{"disambiguationData":[TD([[subQ2,-1.0]])],"derivedFrom":subQ1}),-1.0]])]});}
            var Q8;
            {var subQ0=sQuery(id+"F4.wireOp",EDGE,"E21.MirrorCS");var subQ1=sQuery(id+"F4.wireOp",EDGE,"E20.MirrorCS");var subQ2=makeQuery(id+"F4.imprint","INTERSECT",VERTEX,{"disambiguationData":[OD(1.0)],"derivedFrom":[subQ1,subQ0]});Q8=makeQuery(id+"F4.imprint","IMPRINT",FACE,{"disambiguationData":[TD([[makeQuery(id+"F4.imprint","IMPRINT",EDGE,{"disambiguationData":[TD([[subQ2,-1.0]])],"derivedFrom":subQ1}),1.0]])]});}
            var Q9;
            {var subQ0=sQuery(id+"F4.wireOp",EDGE,"E25.MirrorCS");var subQ1=sQuery(id+"F4.wireOp",EDGE,"E20.MirrorCS");var subQ2=makeQuery(id+"F4.imprint","INTERSECT",VERTEX,{"derivedFrom":[subQ1,subQ0]});Q9=makeQuery(id+"F4.imprint","IMPRINT",FACE,{"disambiguationData":[TD([[makeQuery(id+"F4.imprint","IMPRINT",EDGE,{"disambiguationData":[TD([[subQ2,-1.0]])],"derivedFrom":subQ1}),-1.0]])]});}
            var Q10;
            {var subQ0=sQuery(id+"F4.wireOp",EDGE,"E24.MirrorCS");var subQ1=sQuery(id+"F4.wireOp",EDGE,"E20.MirrorCS");var subQ2=makeQuery(id+"F4.imprint","INTERSECT",VERTEX,{"disambiguationData":[OD(1.0)],"derivedFrom":[subQ1,subQ0]});Q10=makeQuery(id+"F4.imprint","IMPRINT",FACE,{"disambiguationData":[TD([[makeQuery(id+"F4.imprint","IMPRINT",EDGE,{"disambiguationData":[TD([[subQ2,-1.0]])],"derivedFrom":subQ1}),1.0]])]});}
            var Q11;
            {var subQ1=sQuery(id+"F4.wireOp",EDGE,"E20.MirrorCS");var subQ3=sQuery(id+"F4.wireOp",EDGE,"E21.MirrorCS");var subQ4=makeQuery(id+"F4.imprint","INTERSECT",VERTEX,{"disambiguationData":[OD(0.0)],"derivedFrom":[subQ1,subQ3]});Q11=makeQuery(id+"F4.imprint","IMPRINT",FACE,{"disambiguationData":[TD([[makeQuery(id+"F4.imprint","IMPRINT",EDGE,{"disambiguationData":[TD([[subQ4,1.0]])],"derivedFrom":subQ3}),-1.0]])]});}
            var Q12;
            {var subQ0=sQuery(id+"F4.wireOp",EDGE,"E24.MirrorCS");var subQ1=sQuery(id+"F4.wireOp",EDGE,"E20.MirrorCS");var subQ2=makeQuery(id+"F4.imprint","INTERSECT",VERTEX,{"disambiguationData":[OD(1.0)],"derivedFrom":[subQ1,subQ0]});Q12=makeQuery(id+"F4.imprint","IMPRINT",FACE,{"disambiguationData":[TD([[makeQuery(id+"F4.imprint","IMPRINT",EDGE,{"disambiguationData":[TD([[subQ2,-1.0]])],"derivedFrom":subQ1}),-1.0]])]});}
            var Q13;
            {var subQ1=sQuery(id+"F4.wireOp",EDGE,"E18");var subQ3=sQuery(id+"F4.wireOp",EDGE,"E19.MirrorCS");var subQ4=makeQuery(id+"F4.imprint","INTERSECT",VERTEX,{"disambiguationData":[OD(0.0)],"derivedFrom":[subQ1,subQ3]});Q13=makeQuery(id+"F4.imprint","IMPRINT",FACE,{"disambiguationData":[TD([[makeQuery(id+"F4.imprint","IMPRINT",EDGE,{"disambiguationData":[TD([[subQ4,1.0]])],"derivedFrom":subQ3}),1.0]])]});}
            var Q14;
            {var subQ0=sQuery(id+"F4.wireOp",EDGE,"E23");var subQ1=sQuery(id+"F4.wireOp",EDGE,"E18");var subQ2=makeQuery(id+"F4.imprint","INTERSECT",VERTEX,{"disambiguationData":[OD(1.0)],"derivedFrom":[subQ1,subQ0]});Q14=makeQuery(id+"F4.imprint","IMPRINT",FACE,{"disambiguationData":[TD([[makeQuery(id+"F4.imprint","IMPRINT",EDGE,{"disambiguationData":[TD([[subQ2,-1.0]])],"derivedFrom":subQ1}),1.0]])]});}
            var Q15;
            {var subQ0=sQuery(id+"F4.wireOp",EDGE,"E23");var subQ1=sQuery(id+"F4.wireOp",EDGE,"E18");var subQ2=makeQuery(id+"F4.imprint","INTERSECT",VERTEX,{"disambiguationData":[OD(1.0)],"derivedFrom":[subQ1,subQ0]});Q15=makeQuery(id+"F4.imprint","IMPRINT",FACE,{"disambiguationData":[TD([[makeQuery(id+"F4.imprint","IMPRINT",EDGE,{"disambiguationData":[TD([[subQ2,-1.0]])],"derivedFrom":subQ1}),-1.0]])]});}
            var Q16;
            {var subQ3=sQuery(id+"F4.wireOp",EDGE,"E18");var subQ7=sQuery(id+"F4.wireOp",EDGE,"E22");var subQ8=makeQuery(id+"F4.imprint","INTERSECT",VERTEX,{"derivedFrom":[subQ3,subQ7]});Q16=makeQuery(id+"F4.imprint","IMPRINT",FACE,{"disambiguationData":[TD([[makeQuery(id+"F4.imprint","IMPRINT",EDGE,{"disambiguationData":[TD([[subQ8,-1.0]])],"derivedFrom":subQ3}),-1.0]])]});}
            var Q17;
            {var subQ3=sQuery(id+"F4.wireOp",EDGE,"E20.MirrorCS");var subQ6=sQuery(id+"F4.wireOp",EDGE,"E25.MirrorCS");var subQ7=makeQuery(id+"F4.imprint","INTERSECT",VERTEX,{"derivedFrom":[subQ3,subQ6]});Q17=makeQuery(id+"F4.imprint","IMPRINT",FACE,{"disambiguationData":[TD([[makeQuery(id+"F4.imprint","IMPRINT",EDGE,{"disambiguationData":[TD([[subQ7,-1.0]])],"derivedFrom":subQ3}),1.0]])]});}
            extrude(context, id + "F8", {"entities" : qUnion([Q0, Q1, Q2, Q3, Q4, Q5, Q6, Q7, Q8, Q9, Q10, Q11, Q12, Q13, Q14, Q15, Q16, Q17]), "operationType" : NewBodyOperationType.REMOVE, "oppositeDirection" : true, "depth" : 25 * mm, "offsetDistance" : 25 * mm});
        }
        {
            var Q0;
            {var subQ1=sQuery(id+"F4.wireOp",EDGE,"E20.MirrorCS");var subQ3=sQuery(id+"F4.wireOp",EDGE,"E24.MirrorCS");var subQ4=makeQuery(id+"F4.imprint","INTERSECT",VERTEX,{"disambiguationData":[OD(3.0)],"derivedFrom":[subQ1,subQ3]});Q0=makeQuery(id+"F4.imprint","IMPRINT",FACE,{"disambiguationData":[TD([[makeQuery(id+"F4.imprint","IMPRINT",EDGE,{"disambiguationData":[TD([[subQ4,1.0]])],"derivedFrom":subQ3}),-1.0]])]});}
            var Q1;
            {var subQ0=sQuery(id+"F4.wireOp",EDGE,"E19.MirrorCS");var subQ5=sQuery(id+"F4.wireOp",EDGE,"E22");var subQ6=makeQuery(id+"F4.imprint","INTERSECT",VERTEX,{"disambiguationData":[OD(3.0)],"derivedFrom":[subQ0,subQ5]});Q1=makeQuery(id+"F4.imprint","IMPRINT",FACE,{"disambiguationData":[TD([[makeQuery(id+"F4.imprint","IMPRINT",EDGE,{"disambiguationData":[TD([[subQ6,1.0]])],"derivedFrom":subQ5}),-1.0]])]});}
            var Q2;
            {var subQ1=sQuery(id+"F4.wireOp",EDGE,"E19.MirrorCS");var subQ3=sQuery(id+"F4.wireOp",EDGE,"E22");var subQ4=makeQuery(id+"F4.imprint","INTERSECT",VERTEX,{"disambiguationData":[OD(3.0)],"derivedFrom":[subQ1,subQ3]});Q2=makeQuery(id+"F4.imprint","IMPRINT",FACE,{"disambiguationData":[TD([[makeQuery(id+"F4.imprint","IMPRINT",EDGE,{"disambiguationData":[TD([[subQ4,-1.0]])],"derivedFrom":subQ3}),-1.0]])]});}
            var Q3;
            {var subQ1=sQuery(id+"F4.wireOp",EDGE,"E18");var subQ3=sQuery(id+"F4.wireOp",EDGE,"E23");var subQ4=makeQuery(id+"F4.imprint","INTERSECT",VERTEX,{"disambiguationData":[OD(3.0)],"derivedFrom":[subQ1,subQ3]});Q3=makeQuery(id+"F4.imprint","IMPRINT",FACE,{"disambiguationData":[TD([[makeQuery(id+"F4.imprint","IMPRINT",EDGE,{"disambiguationData":[TD([[subQ4,-1.0]])],"derivedFrom":subQ3}),1.0]])]});}
            var Q4;
            {var subQ0=sQuery(id+"F4.wireOp",EDGE,"E19.MirrorCS");var subQ1=sQuery(id+"F4.wireOp",EDGE,"E18");var subQ2=makeQuery(id+"F4.imprint","INTERSECT",VERTEX,{"disambiguationData":[OD(1.0)],"derivedFrom":[subQ1,subQ0]});Q4=makeQuery(id+"F4.imprint","IMPRINT",FACE,{"disambiguationData":[TD([[makeQuery(id+"F4.imprint","IMPRINT",EDGE,{"disambiguationData":[TD([[subQ2,-1.0]])],"derivedFrom":subQ1}),1.0]])]});}
            var Q5;
            {var subQ0=sQuery(id+"F4.wireOp",EDGE,"E19.MirrorCS");var subQ1=sQuery(id+"F4.wireOp",EDGE,"E18");var subQ2=makeQuery(id+"F4.imprint","INTERSECT",VERTEX,{"disambiguationData":[OD(1.0)],"derivedFrom":[subQ1,subQ0]});Q5=makeQuery(id+"F4.imprint","IMPRINT",FACE,{"disambiguationData":[TD([[makeQuery(id+"F4.imprint","IMPRINT",EDGE,{"disambiguationData":[TD([[subQ2,-1.0]])],"derivedFrom":subQ1}),-1.0]])]});}
            var Q6;
            {var subQ0=sQuery(id+"F4.wireOp",EDGE,"E22");var subQ1=sQuery(id+"F4.wireOp",EDGE,"E18");var subQ2=makeQuery(id+"F4.imprint","INTERSECT",VERTEX,{"derivedFrom":[subQ1,subQ0]});Q6=makeQuery(id+"F4.imprint","IMPRINT",FACE,{"disambiguationData":[TD([[makeQuery(id+"F4.imprint","IMPRINT",EDGE,{"disambiguationData":[TD([[subQ2,-1.0]])],"derivedFrom":subQ1}),1.0]])]});}
            var Q7;
            {var subQ0=sQuery(id+"F4.wireOp",EDGE,"E23");var subQ1=sQuery(id+"F4.wireOp",EDGE,"E18");var subQ2=makeQuery(id+"F4.imprint","INTERSECT",VERTEX,{"disambiguationData":[OD(1.0)],"derivedFrom":[subQ1,subQ0]});Q7=makeQuery(id+"F4.imprint","IMPRINT",FACE,{"disambiguationData":[TD([[makeQuery(id+"F4.imprint","IMPRINT",EDGE,{"disambiguationData":[TD([[subQ2,-1.0]])],"derivedFrom":subQ1}),1.0]])]});}
            var Q8;
            {var subQ0=sQuery(id+"F4.wireOp",EDGE,"E23");var subQ1=sQuery(id+"F4.wireOp",EDGE,"E18");var subQ2=makeQuery(id+"F4.imprint","INTERSECT",VERTEX,{"disambiguationData":[OD(1.0)],"derivedFrom":[subQ1,subQ0]});Q8=makeQuery(id+"F4.imprint","IMPRINT",FACE,{"disambiguationData":[TD([[makeQuery(id+"F4.imprint","IMPRINT",EDGE,{"disambiguationData":[TD([[subQ2,-1.0]])],"derivedFrom":subQ1}),-1.0]])]});}
            var Q9;
            {var subQ1=sQuery(id+"F4.wireOp",EDGE,"E18");var subQ3=sQuery(id+"F4.wireOp",EDGE,"E19.MirrorCS");var subQ4=makeQuery(id+"F4.imprint","INTERSECT",VERTEX,{"disambiguationData":[OD(0.0)],"derivedFrom":[subQ1,subQ3]});Q9=makeQuery(id+"F4.imprint","IMPRINT",FACE,{"disambiguationData":[TD([[makeQuery(id+"F4.imprint","IMPRINT",EDGE,{"disambiguationData":[TD([[subQ4,1.0]])],"derivedFrom":subQ3}),1.0]])]});}
            var Q10;
            {var subQ0=sQuery(id+"F4.wireOp",EDGE,"E21.MirrorCS");var subQ1=sQuery(id+"F4.wireOp",EDGE,"E20.MirrorCS");var subQ2=makeQuery(id+"F4.imprint","INTERSECT",VERTEX,{"disambiguationData":[OD(1.0)],"derivedFrom":[subQ1,subQ0]});Q10=makeQuery(id+"F4.imprint","IMPRINT",FACE,{"disambiguationData":[TD([[makeQuery(id+"F4.imprint","IMPRINT",EDGE,{"disambiguationData":[TD([[subQ2,-1.0]])],"derivedFrom":subQ1}),-1.0]])]});}
            var Q11;
            {var subQ0=sQuery(id+"F4.wireOp",EDGE,"E21.MirrorCS");var subQ1=sQuery(id+"F4.wireOp",EDGE,"E20.MirrorCS");var subQ2=makeQuery(id+"F4.imprint","INTERSECT",VERTEX,{"disambiguationData":[OD(1.0)],"derivedFrom":[subQ1,subQ0]});Q11=makeQuery(id+"F4.imprint","IMPRINT",FACE,{"disambiguationData":[TD([[makeQuery(id+"F4.imprint","IMPRINT",EDGE,{"disambiguationData":[TD([[subQ2,-1.0]])],"derivedFrom":subQ1}),1.0]])]});}
            var Q12;
            {var subQ0=sQuery(id+"F4.wireOp",EDGE,"E25.MirrorCS");var subQ1=sQuery(id+"F4.wireOp",EDGE,"E20.MirrorCS");var subQ2=makeQuery(id+"F4.imprint","INTERSECT",VERTEX,{"derivedFrom":[subQ1,subQ0]});Q12=makeQuery(id+"F4.imprint","IMPRINT",FACE,{"disambiguationData":[TD([[makeQuery(id+"F4.imprint","IMPRINT",EDGE,{"disambiguationData":[TD([[subQ2,-1.0]])],"derivedFrom":subQ1}),-1.0]])]});}
            var Q13;
            {var subQ1=sQuery(id+"F4.wireOp",EDGE,"E20.MirrorCS");var subQ3=sQuery(id+"F4.wireOp",EDGE,"E21.MirrorCS");var subQ4=makeQuery(id+"F4.imprint","INTERSECT",VERTEX,{"disambiguationData":[OD(0.0)],"derivedFrom":[subQ1,subQ3]});Q13=makeQuery(id+"F4.imprint","IMPRINT",FACE,{"disambiguationData":[TD([[makeQuery(id+"F4.imprint","IMPRINT",EDGE,{"disambiguationData":[TD([[subQ4,1.0]])],"derivedFrom":subQ3}),-1.0]])]});}
            var Q14;
            {var subQ0=sQuery(id+"F4.wireOp",EDGE,"E24.MirrorCS");var subQ1=sQuery(id+"F4.wireOp",EDGE,"E20.MirrorCS");var subQ2=makeQuery(id+"F4.imprint","INTERSECT",VERTEX,{"disambiguationData":[OD(1.0)],"derivedFrom":[subQ1,subQ0]});Q14=makeQuery(id+"F4.imprint","IMPRINT",FACE,{"disambiguationData":[TD([[makeQuery(id+"F4.imprint","IMPRINT",EDGE,{"disambiguationData":[TD([[subQ2,-1.0]])],"derivedFrom":subQ1}),1.0]])]});}
            var Q15;
            {var subQ0=sQuery(id+"F4.wireOp",EDGE,"E24.MirrorCS");var subQ1=sQuery(id+"F4.wireOp",EDGE,"E20.MirrorCS");var subQ2=makeQuery(id+"F4.imprint","INTERSECT",VERTEX,{"disambiguationData":[OD(1.0)],"derivedFrom":[subQ1,subQ0]});Q15=makeQuery(id+"F4.imprint","IMPRINT",FACE,{"disambiguationData":[TD([[makeQuery(id+"F4.imprint","IMPRINT",EDGE,{"disambiguationData":[TD([[subQ2,-1.0]])],"derivedFrom":subQ1}),-1.0]])]});}
            var Q16;
            {var subQ3=sQuery(id+"F4.wireOp",EDGE,"E20.MirrorCS");var subQ6=sQuery(id+"F4.wireOp",EDGE,"E25.MirrorCS");var subQ7=makeQuery(id+"F4.imprint","INTERSECT",VERTEX,{"derivedFrom":[subQ3,subQ6]});Q16=makeQuery(id+"F4.imprint","IMPRINT",FACE,{"disambiguationData":[TD([[makeQuery(id+"F4.imprint","IMPRINT",EDGE,{"disambiguationData":[TD([[subQ7,-1.0]])],"derivedFrom":subQ3}),1.0]])]});}
            var Q17;
            {var subQ3=sQuery(id+"F4.wireOp",EDGE,"E18");var subQ7=sQuery(id+"F4.wireOp",EDGE,"E22");var subQ8=makeQuery(id+"F4.imprint","INTERSECT",VERTEX,{"derivedFrom":[subQ3,subQ7]});Q17=makeQuery(id+"F4.imprint","IMPRINT",FACE,{"disambiguationData":[TD([[makeQuery(id+"F4.imprint","IMPRINT",EDGE,{"disambiguationData":[TD([[subQ8,-1.0]])],"derivedFrom":subQ3}),-1.0]])]});}
            extrude(context, id + "F9", {"entities" : qUnion([Q0, Q1, Q2, Q3, Q4, Q5, Q6, Q7, Q8, Q9, Q10, Q11, Q12, Q13, Q14, Q15, Q16, Q17]), "operationType" : NewBodyOperationType.REMOVE, "oppositeDirection" : true, "depth" : -25 * mm, "offsetDistance" : 25 * mm});
        }
    });
